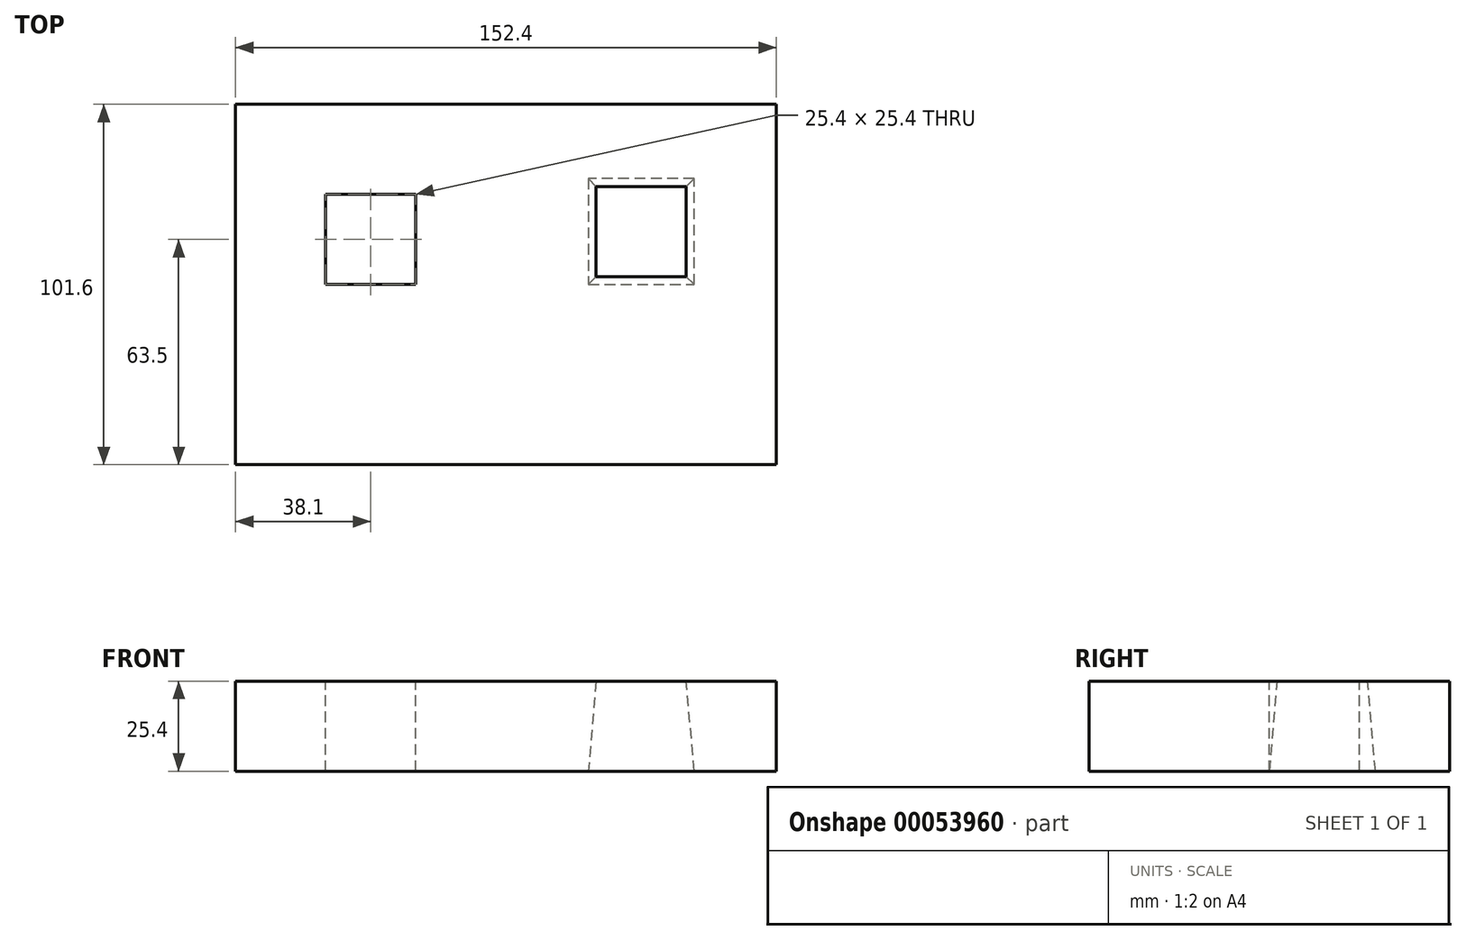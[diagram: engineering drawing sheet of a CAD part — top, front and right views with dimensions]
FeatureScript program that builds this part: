
annotation { "Feature Type Name" : "Feature", "Feature Type Description" : "" }
export const myFeature = defineFeature(function(context is Context, id is Id, definition is map)
    precondition{}
    {
        {
            var Q0;
            Q0=qCreatedBy(makeId("Top.planeOp"),FACE);
            var sketch = newSketch(context, id + "F0", { "sketchPlane" : qUnion([Q0])});
            skLineSegment(sketch, "E0.rect.bottom", {"start": v(-76.2, 50.8) * mm, "end": v(76.2, 50.8) * mm});
            skLineSegment(sketch, "E0.rect.top", {"start": v(-76.2, -50.8) * mm, "end": v(76.2, -50.8) * mm});
            skLineSegment(sketch, "E0.rect.left", {"start": v(-76.2, 50.8) * mm, "end": v(-76.2, -50.8) * mm});
            skLineSegment(sketch, "E0.rect.right", {"start": v(76.2, 50.8) * mm, "end": v(76.2, -50.8) * mm});
            skPoint(sketch, "E0.rect.middle", {"position": v(0, 0) * mm});
            skSolve(sketch);
        }
        {
            var Q0;
            Q0 = qSketchRegion(id + "F0", true);
            extrude(context, id + "F1", {"entities" : qUnion([Q0]), "depth" : 25.4 * mm});
        }
        {
            var Q0;
            Q0=makeQuery(id+"F1.opExtrude","CAP_FACE",FACE,{"disambiguationData":[OSD([sQuery(id+"F0.wireOp",EDGE,"E0.rect.bottom"),sQuery(id+"F0.wireOp",EDGE,"E0.rect.top"),sQuery(id+"F0.wireOp",EDGE,"E0.rect.left"),sQuery(id+"F0.wireOp",EDGE,"E0.rect.right")])],"isStart":false});
            var sketch = newSketch(context, id + "F2", { "sketchPlane" : qUnion([Q0])});
            skLineSegment(sketch, "E1.rect.bottom", {"start": v(-25.4, 0) * mm, "end": v(-50.8, 0) * mm});
            skLineSegment(sketch, "E1.rect.top", {"start": v(-25.4, 25.4) * mm, "end": v(-50.8, 25.4) * mm});
            skLineSegment(sketch, "E1.rect.left", {"start": v(-25.4, 0) * mm, "end": v(-25.4, 25.4) * mm});
            skLineSegment(sketch, "E1.rect.right", {"start": v(-50.8, 0) * mm, "end": v(-50.8, 25.4) * mm});
            skPoint(sketch, "E1.rect.middle", {"position": v(-38.1, 12.7) * mm});
            skSolve(sketch);
        }
        {
            var Q0;
            Q0 = qSketchRegion(id + "F2", true);
            extrude(context, id + "F3", {"entities" : qUnion([Q0]), "operationType" : NewBodyOperationType.REMOVE, "endBound" : BoundingType.THROUGH_ALL, "oppositeDirection" : true, "depth" : 25.4 * mm});
        }
        {
            var Q0;
            Q0=makeQuery(id+"F1.opExtrude","CAP_FACE",FACE,{"disambiguationData":[OSD([sQuery(id+"F0.wireOp",EDGE,"E0.rect.bottom"),sQuery(id+"F0.wireOp",EDGE,"E0.rect.top"),sQuery(id+"F0.wireOp",EDGE,"E0.rect.left"),sQuery(id+"F0.wireOp",EDGE,"E0.rect.right")])],"isStart":false});
            var sketch = newSketch(context, id + "F4", { "sketchPlane" : qUnion([Q0])});
            skLineSegment(sketch, "E2.rect.bottom", {"start": v(25.4, 27.65) * mm, "end": v(50.8, 27.65) * mm});
            skLineSegment(sketch, "E2.rect.top", {"start": v(25.4, 2.25) * mm, "end": v(50.8, 2.25) * mm});
            skLineSegment(sketch, "E2.rect.left", {"start": v(25.4, 27.65) * mm, "end": v(25.4, 2.25) * mm});
            skLineSegment(sketch, "E2.rect.right", {"start": v(50.8, 27.65) * mm, "end": v(50.8, 2.25) * mm});
            skPoint(sketch, "E2.rect.middle", {"position": v(38.1, 14.95) * mm});
            skSolve(sketch);
        }
        {
            var Q0;
            Q0 = qSketchRegion(id + "F4", true);
            extrude(context, id + "F5", {"entities" : qUnion([Q0]), "operationType" : NewBodyOperationType.REMOVE, "endBound" : BoundingType.THROUGH_ALL, "oppositeDirection" : true, "depth" : 25.4 * mm, "hasDraft" : true, "draftAngle" : 5 * degree});
        }
    });
